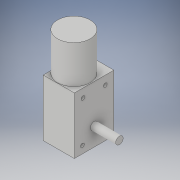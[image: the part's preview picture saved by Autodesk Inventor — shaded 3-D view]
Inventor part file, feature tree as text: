
AUTODESK INVENTOR PART (.ipt)
format: ipt  version: 2019 (Build 230136000, 136)  size: 141,824 bytes
history: native  units: in
note: dims shown in document units (in); Inventor stores cm internally (conversion verified against a paired STEP export)
features: extrude x4, sketch x4
ambient origin geometry x8: Origin, YZ Plane, XZ Plane, XY Plane, X Axis, Y Axis, Z Axis, Center Point
bodies: Solid1 (feature_tree)
feature tree (8):
  extrude  "Extrusion1"  Depth=1.2598in
  extrude  "Extrusion2"  Depth=0.9921in
  extrude  "Extrusion3"  Depth=0.725in
  extrude  "Extrusion4"  Depth=0.1181in
  sketch  "Sketch1"  dims[d0=1.811in d1=1.2598in]
  sketch  "Sketch3"  dims[d2=0.9921in d3=0.0in d4=1.0394in]
  sketch  "Sketch4"  dims[d5=0.55in d6=0.725in]
  sketch  "Sketch5"  dims[d7=1.2126in d8=0.0in d9=0.1181in d10=0.1181in d11=0.1181in d12=0.1181in d13=0.2756in d14=0.2756in d15=0.7087in d16=1.2992in d17=1.2992in d18=0.7087in d19=0.2756in d20=0.2953in d21=0.1969in d22=0.0in d23=0.2362in d24=0.63in d25=0.5906in d26=0.8071in d27=0.0in]
